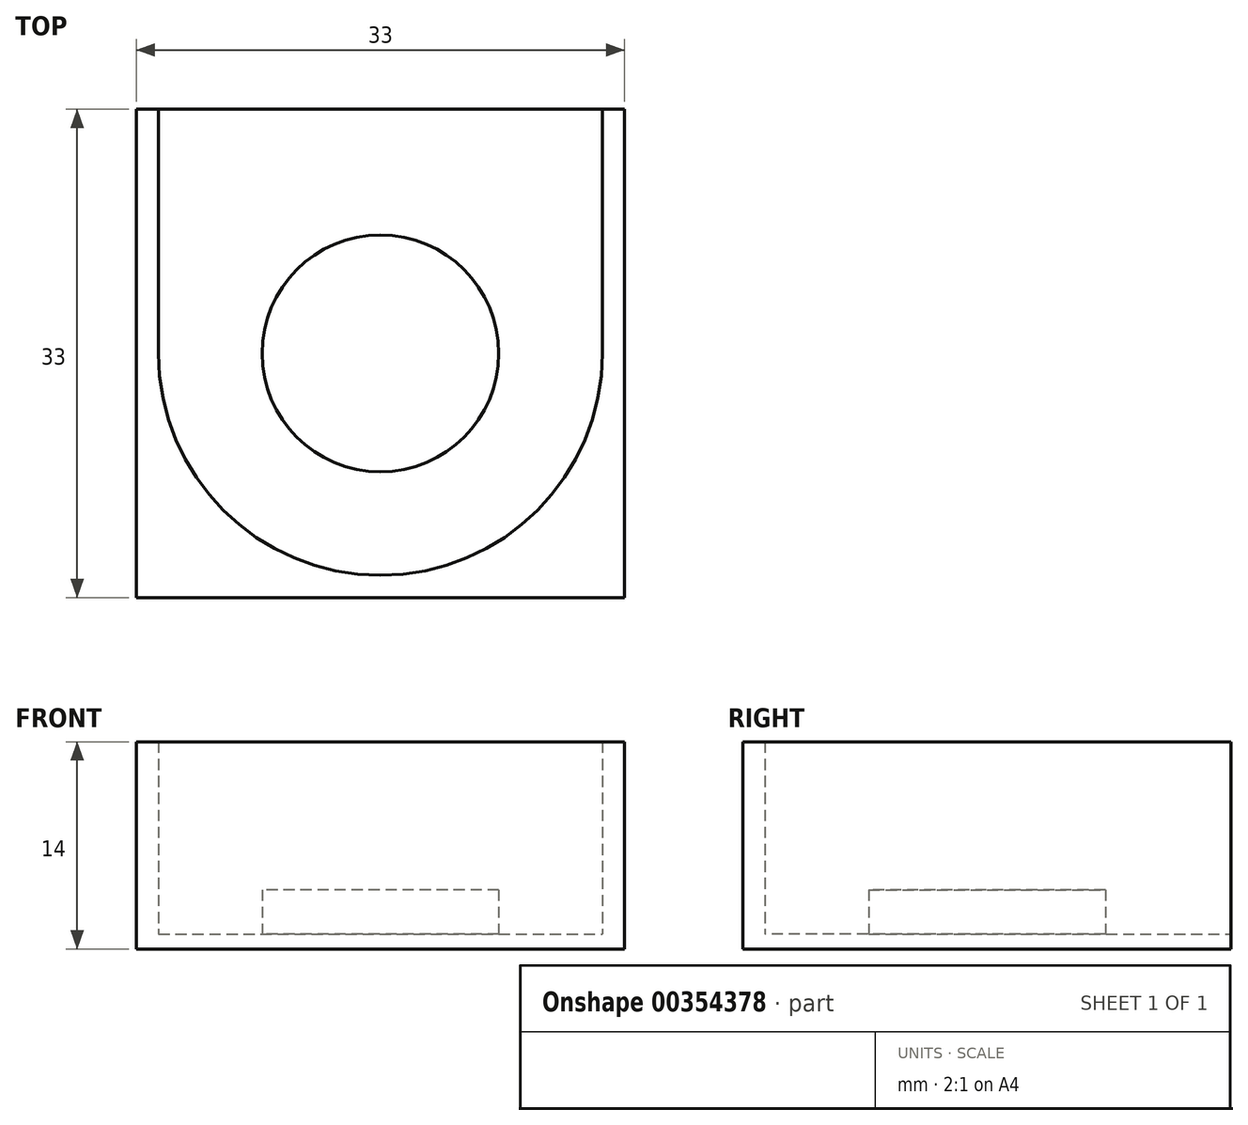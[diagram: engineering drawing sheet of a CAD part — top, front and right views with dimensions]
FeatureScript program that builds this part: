
annotation { "Feature Type Name" : "Feature", "Feature Type Description" : "" }
export const myFeature = defineFeature(function(context is Context, id is Id, definition is map)
    precondition{}
    {
        {
            var Q0;
            Q0=qCreatedBy(makeId("Top.planeOp"),FACE);
            var sketch = newSketch(context, id + "F0", { "sketchPlane" : qUnion([Q0])});
            skLineSegment(sketch, "E0.bottom", {"start": v(-16.5, 16.5) * mm, "end": v(16.5, 16.5) * mm});
            skLineSegment(sketch, "E0.top", {"start": v(-16.5, -16.5) * mm, "end": v(16.5, -16.5) * mm});
            skLineSegment(sketch, "E0.left", {"start": v(-16.5, 16.5) * mm, "end": v(-16.5, -16.5) * mm});
            skLineSegment(sketch, "E0.right", {"start": v(16.5, 16.5) * mm, "end": v(16.5, -16.5) * mm});
            skLineSegment(sketch, "E1", {"start": v(-16.5, 16.5) * mm, "end": v(16.5, -16.5) * mm, "construction": true});
            skPoint(sketch, "E2", {"position": v(0, 0) * mm});
            skCircle(sketch, "E3", {"center": v(0, 0) * mm, "radius": 8 * mm});
            skSolve(sketch);
        }
        {
            var Q0;
            Q0=makeQuery(id+"F0.imprint","IMPRINT",FACE,{"disambiguationData":[TD([[makeQuery(id+"F0.imprint","IMPRINT",EDGE,{"derivedFrom":sQuery(id+"F0.wireOp",EDGE,"E3")}),1.0]])]});
            var Q1;
            Q1=makeQuery(id+"F0.imprint","IMPRINT",FACE,{"disambiguationData":[TD([[makeQuery(id+"F0.imprint","IMPRINT",EDGE,{"derivedFrom":sQuery(id+"F0.wireOp",EDGE,"E0.bottom")}),-1.0]])]});
            extrude(context, id + "F1", {"entities" : qUnion([Q0, Q1]), "oppositeDirection" : true, "depth" : 1 * mm});
        }
        {
            var Q0;
            Q0=makeQuery(id+"F0.imprint","IMPRINT",FACE,{"disambiguationData":[TD([[makeQuery(id+"F0.imprint","IMPRINT",EDGE,{"derivedFrom":sQuery(id+"F0.wireOp",EDGE,"E3")}),1.0]])]});
            extrude(context, id + "F2", {"entities" : qUnion([Q0]), "operationType" : NewBodyOperationType.ADD, "depth" : 3 * mm});
        }
        {
            var Q0;
            Q0=makeQuery(id+"F0.imprint","IMPRINT",FACE,{"disambiguationData":[TD([[makeQuery(id+"F0.imprint","IMPRINT",EDGE,{"derivedFrom":sQuery(id+"F0.wireOp",EDGE,"E0.bottom")}),-1.0]])]});
            var sketch = newSketch(context, id + "F3", { "sketchPlane" : qUnion([Q0])});
            skArc(sketch, "E4", {"start": v(-15, 0) * mm, "mid": v(0, -15) * mm, "end": v(15, 0) * mm});
            skLineSegment(sketch, "E5.0", {"start": v(-16.5, 16.5) * mm, "end": v(-16.5, -16.5) * mm});
            skLineSegment(sketch, "E6.0", {"start": v(-16.5, -16.5) * mm, "end": v(16.5, -16.5) * mm});
            skLineSegment(sketch, "E7.0", {"start": v(16.5, 16.5) * mm, "end": v(16.5, -16.5) * mm});
            skLineSegment(sketch, "E8", {"start": v(-15, 0) * mm, "end": v(-15, 16.5) * mm});
            skLineSegment(sketch, "E9", {"start": v(15, 0) * mm, "end": v(15, 16.5) * mm});
            skLineSegment(sketch, "E10", {"start": v(-16.5, 16.5) * mm, "end": v(-15, 16.5) * mm});
            skLineSegment(sketch, "E11", {"start": v(15, 16.5) * mm, "end": v(16.5, 16.5) * mm});
            skSolve(sketch);
        }
        {
            var Q0;
            Q0 = qSketchRegion(id + "F3", true);
            extrude(context, id + "F4", {"entities" : qUnion([Q0]), "operationType" : NewBodyOperationType.ADD, "depth" : 13 * mm});
        }
    });
